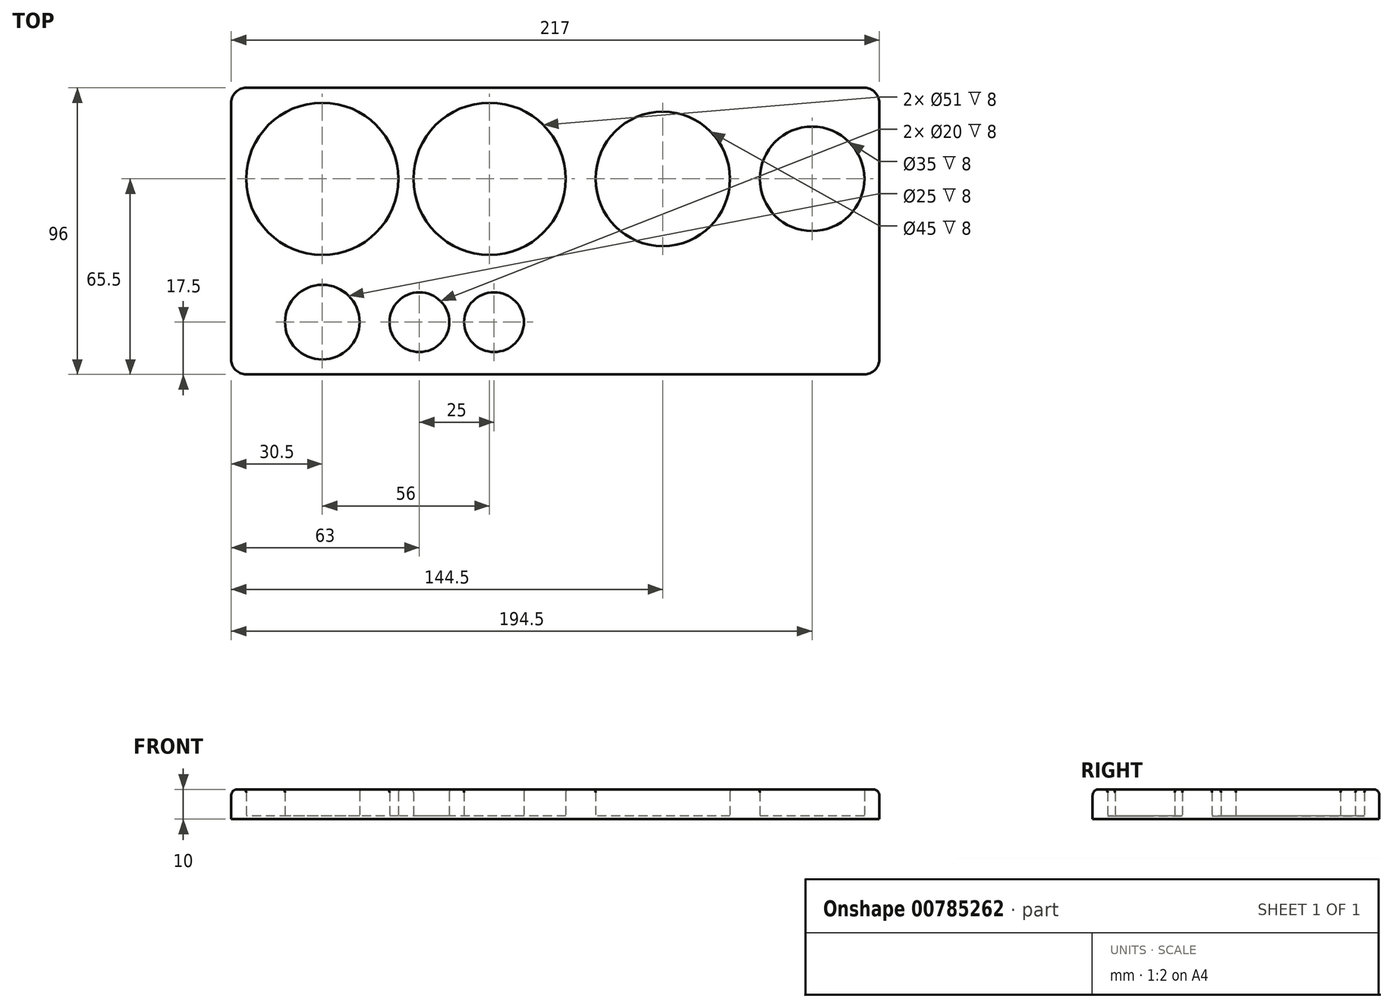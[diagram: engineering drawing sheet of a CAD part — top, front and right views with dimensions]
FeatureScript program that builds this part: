
annotation { "Feature Type Name" : "Feature", "Feature Type Description" : "" }
export const myFeature = defineFeature(function(context is Context, id is Id, definition is map)
    precondition{}
    {
        {
            var Q0;
            Q0=qCreatedBy(makeId("Top.planeOp"),FACE);
            var sketch = newSketch(context, id + "F0", { "sketchPlane" : qUnion([Q0])});
            skLineSegment(sketch, "E0.bottom", {"start": v(-108.5, 48) * mm, "end": v(108.5, 48) * mm});
            skLineSegment(sketch, "E0.top", {"start": v(-108.5, -48) * mm, "end": v(108.5, -48) * mm});
            skLineSegment(sketch, "E0.left", {"start": v(-108.5, 48) * mm, "end": v(-108.5, -48) * mm});
            skLineSegment(sketch, "E0.right", {"start": v(108.5, 48) * mm, "end": v(108.5, -48) * mm});
            skPoint(sketch, "E0.middle", {"position": v(0, 0) * mm});
            skCircle(sketch, "E1", {"center": v(-78, 17.5) * mm, "radius": 25.5 * mm});
            skCircle(sketch, "E2", {"center": v(-22, 17.5) * mm, "radius": 25.5 * mm});
            skCircle(sketch, "E3", {"center": v(86, 17.5) * mm, "radius": 17.5 * mm});
            skCircle(sketch, "E4", {"center": v(-78, -30.5) * mm, "radius": 12.5 * mm});
            skCircle(sketch, "E5", {"center": v(36, 17.5) * mm, "radius": 22.5 * mm});
            skCircle(sketch, "E6", {"center": v(-45.5, -30.5) * mm, "radius": 10 * mm});
            skCircle(sketch, "E7", {"center": v(-20.5, -30.5) * mm, "radius": 10 * mm});
            skLineSegment(sketch, "E8", {"start": v(-108.5, 17.5) * mm, "end": v(108.5, 17.5) * mm, "construction": true});
            skSolve(sketch);
        }
        {
            var Q0;
            Q0=makeQuery(id+"F0.imprint","IMPRINT",FACE,{"disambiguationData":[TD([[makeQuery(id+"F0.imprint","IMPRINT",EDGE,{"derivedFrom":sQuery(id+"F0.wireOp",EDGE,"E0.bottom")}),-1.0]])]});
            extrude(context, id + "F1", {"entities" : qUnion([Q0]), "depth" : 10 * mm, "offsetDistance" : 25 * mm});
        }
        {
            var Q0;
            Q0=makeQuery(id+"F0.imprint","IMPRINT",FACE,{"disambiguationData":[TD([[makeQuery(id+"F0.imprint","IMPRINT",EDGE,{"derivedFrom":sQuery(id+"F0.wireOp",EDGE,"E1")}),1.0]])]});
            var Q1;
            Q1=makeQuery(id+"F0.imprint","IMPRINT",FACE,{"disambiguationData":[TD([[makeQuery(id+"F0.imprint","IMPRINT",EDGE,{"derivedFrom":sQuery(id+"F0.wireOp",EDGE,"E2")}),1.0]])]});
            var Q2;
            Q2=makeQuery(id+"F0.imprint","IMPRINT",FACE,{"disambiguationData":[TD([[makeQuery(id+"F0.imprint","IMPRINT",EDGE,{"derivedFrom":sQuery(id+"F0.wireOp",EDGE,"E5")}),1.0]])]});
            var Q3;
            Q3=makeQuery(id+"F0.imprint","IMPRINT",FACE,{"disambiguationData":[TD([[makeQuery(id+"F0.imprint","IMPRINT",EDGE,{"derivedFrom":sQuery(id+"F0.wireOp",EDGE,"E3")}),1.0]])]});
            var Q4;
            Q4=makeQuery(id+"F0.imprint","IMPRINT",FACE,{"disambiguationData":[TD([[makeQuery(id+"F0.imprint","IMPRINT",EDGE,{"derivedFrom":sQuery(id+"F0.wireOp",EDGE,"E4")}),1.0]])]});
            var Q5;
            Q5=makeQuery(id+"F0.imprint","IMPRINT",FACE,{"disambiguationData":[TD([[makeQuery(id+"F0.imprint","IMPRINT",EDGE,{"derivedFrom":sQuery(id+"F0.wireOp",EDGE,"E6")}),1.0]])]});
            var Q6;
            Q6=makeQuery(id+"F0.imprint","IMPRINT",FACE,{"disambiguationData":[TD([[makeQuery(id+"F0.imprint","IMPRINT",EDGE,{"derivedFrom":sQuery(id+"F0.wireOp",EDGE,"E7")}),1.0]])]});
            extrude(context, id + "F2", {"entities" : qUnion([Q0, Q1, Q2, Q3, Q4, Q5, Q6]), "operationType" : NewBodyOperationType.ADD, "depth" : 1 * mm, "offsetDistance" : 25 * mm});
        }
        {
            var Q0;
            Q0=makeQuery(id+"F1.opExtrude","CAP_EDGE",EDGE,{"disambiguationData":[OSD([sQuery(id+"F0.wireOp",EDGE,"E1")])],"isStart":false});
            var Q1;
            Q1=makeQuery(id+"F1.opExtrude","CAP_EDGE",EDGE,{"disambiguationData":[OSD([sQuery(id+"F0.wireOp",EDGE,"E2")])],"isStart":false});
            var Q2;
            Q2=makeQuery(id+"F1.opExtrude","CAP_EDGE",EDGE,{"disambiguationData":[OSD([sQuery(id+"F0.wireOp",EDGE,"E5")])],"isStart":false});
            var Q3;
            Q3=makeQuery(id+"F1.opExtrude","CAP_EDGE",EDGE,{"disambiguationData":[OSD([sQuery(id+"F0.wireOp",EDGE,"E3")])],"isStart":false});
            var Q4;
            Q4=makeQuery(id+"F1.opExtrude","CAP_EDGE",EDGE,{"disambiguationData":[OSD([sQuery(id+"F0.wireOp",EDGE,"E4")])],"isStart":false});
            var Q5;
            Q5=makeQuery(id+"F1.opExtrude","CAP_EDGE",EDGE,{"disambiguationData":[OSD([sQuery(id+"F0.wireOp",EDGE,"E6")])],"isStart":false});
            var Q6;
            Q6=makeQuery(id+"F1.opExtrude","CAP_EDGE",EDGE,{"disambiguationData":[OSD([sQuery(id+"F0.wireOp",EDGE,"E7")])],"isStart":false});
            fillet(context, id + "F3", {"entities" : qUnion([Q0, Q1, Q2, Q3, Q4, Q5, Q6]), "radius" : 1 * mm, "tangentPropagation" : true, "allowEdgeOverflow" : false});
        }
        {
            var Q0;
            Q0=makeQuery(id+"F1.opExtrude","CAP_EDGE",EDGE,{"disambiguationData":[OSD([sQuery(id+"F0.wireOp",EDGE,"E0.left")])],"isStart":false});
            var Q1;
            Q1=makeQuery(id+"F1.opExtrude","CAP_EDGE",EDGE,{"disambiguationData":[OSD([sQuery(id+"F0.wireOp",EDGE,"E0.bottom")])],"isStart":false});
            var Q2;
            Q2=makeQuery(id+"F1.opExtrude","CAP_EDGE",EDGE,{"disambiguationData":[OSD([sQuery(id+"F0.wireOp",EDGE,"E0.right")])],"isStart":false});
            var Q3;
            Q3=makeQuery(id+"F1.opExtrude","CAP_EDGE",EDGE,{"disambiguationData":[OSD([sQuery(id+"F0.wireOp",EDGE,"E0.top")])],"isStart":false});
            fillet(context, id + "F4", {"entities" : qUnion([Q0, Q1, Q2, Q3]), "radius" : 2 * mm, "tangentPropagation" : true, "allowEdgeOverflow" : false});
        }
        {
            var Q0;
            Q0=makeQuery(id+"F1.opExtrude","SWEPT_EDGE",EDGE,{"disambiguationData":[OSD([sQuery(id+"F0.wireOp",EDGE,"E0.top"),sQuery(id+"F0.wireOp",EDGE,"E0.left")])]});
            var Q1;
            Q1=makeQuery(id+"F4.opFillet","BLEND_EDGE",EDGE,{"blendedFrom":[makeQuery(id+"F1.opExtrude","CAP_EDGE",EDGE,{"disambiguationData":[OSD([sQuery(id+"F0.wireOp",EDGE,"E0.top")])],"isStart":false}),makeQuery(id+"F1.opExtrude","CAP_EDGE",EDGE,{"disambiguationData":[OSD([sQuery(id+"F0.wireOp",EDGE,"E0.left")])],"isStart":false})],"blendedInto":[]});
            var Q2;
            Q2=makeQuery(id+"F1.opExtrude","SWEPT_EDGE",EDGE,{"disambiguationData":[OSD([sQuery(id+"F0.wireOp",EDGE,"E0.bottom"),sQuery(id+"F0.wireOp",EDGE,"E0.left")])]});
            var Q3;
            Q3=makeQuery(id+"F4.opFillet","BLEND_EDGE",EDGE,{"blendedFrom":[makeQuery(id+"F1.opExtrude","CAP_EDGE",EDGE,{"disambiguationData":[OSD([sQuery(id+"F0.wireOp",EDGE,"E0.bottom")])],"isStart":false}),makeQuery(id+"F1.opExtrude","CAP_EDGE",EDGE,{"disambiguationData":[OSD([sQuery(id+"F0.wireOp",EDGE,"E0.left")])],"isStart":false})],"blendedInto":[]});
            var Q4;
            Q4=makeQuery(id+"F1.opExtrude","SWEPT_EDGE",EDGE,{"disambiguationData":[OSD([sQuery(id+"F0.wireOp",EDGE,"E0.bottom"),sQuery(id+"F0.wireOp",EDGE,"E0.right")])]});
            var Q5;
            Q5=makeQuery(id+"F4.opFillet","BLEND_EDGE",EDGE,{"blendedFrom":[makeQuery(id+"F1.opExtrude","CAP_EDGE",EDGE,{"disambiguationData":[OSD([sQuery(id+"F0.wireOp",EDGE,"E0.bottom")])],"isStart":false}),makeQuery(id+"F1.opExtrude","CAP_EDGE",EDGE,{"disambiguationData":[OSD([sQuery(id+"F0.wireOp",EDGE,"E0.right")])],"isStart":false})],"blendedInto":[]});
            var Q6;
            Q6=makeQuery(id+"F1.opExtrude","SWEPT_EDGE",EDGE,{"disambiguationData":[OSD([sQuery(id+"F0.wireOp",EDGE,"E0.top"),sQuery(id+"F0.wireOp",EDGE,"E0.right")])]});
            var Q7;
            Q7=makeQuery(id+"F4.opFillet","BLEND_EDGE",EDGE,{"blendedFrom":[makeQuery(id+"F1.opExtrude","CAP_EDGE",EDGE,{"disambiguationData":[OSD([sQuery(id+"F0.wireOp",EDGE,"E0.top")])],"isStart":false}),makeQuery(id+"F1.opExtrude","CAP_EDGE",EDGE,{"disambiguationData":[OSD([sQuery(id+"F0.wireOp",EDGE,"E0.right")])],"isStart":false})],"blendedInto":[]});
            fillet(context, id + "F5", {"entities" : qUnion([Q0, Q1, Q2, Q3, Q4, Q5, Q6, Q7]), "radius" : 5 * mm, "tangentPropagation" : true, "allowEdgeOverflow" : false});
        }
    });
